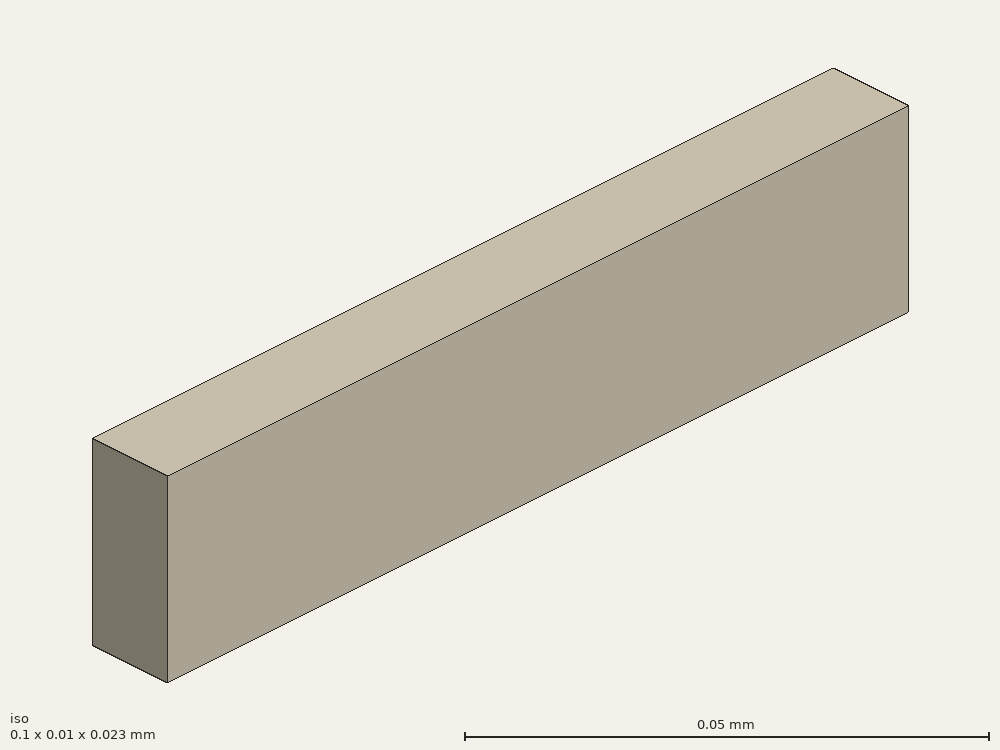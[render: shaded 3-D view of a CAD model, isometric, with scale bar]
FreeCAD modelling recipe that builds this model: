
FCSTD DOCUMENT  (FreeCAD 0.21R33694 (Git))
Label: straight-rotated
License: All rights reserved
LicenseURL: http://en.wikipedia.org/wiki/All_rights_reserved
objects: Part::Part2DObjectPython×5, App::FeaturePython×4, Part::Extrusion×1
note: 6 computed .brp shape members not serialized (recipe doc carries the construction recipe); baked Part::Feature solids carry a one-line shape summary decoded from their .brp

FEATURE [Part::Part2DObjectPython] Rectangle001  label="_Pport1"  # Draft 2D object (typed FeaturePython)
  Area = 0.000232258
  ChamferSize = 0
  Columns = 1
  FilletRadius = 0
  Height = 0.01016
  Length = 0.02286
  MakeFace = true
  Placement = pos=(-0.1,-0.00508,-0.01143) rot=(0,-1,0;1.5708rad)
  Rows = 1
FEATURE [Part::Part2DObjectPython] Line  label="_Pv1"  # Draft 2D object (typed FeaturePython)
  Area = 0
  ChamferSize = 0
  Closed = false
  End = (-0.1,0.00508,-1.8e-15)
  FilletRadius = 0
  Length = 0.01016
  MakeFace = true
  Placement = pos=(-0.1,-0.00508,0) rot=(0,-1,0;1.5708rad)
  Points = (2) [(0,0,0),(-1.77605e-15,0.01016,0)]
  Start = (-0.1,-0.00508,0)
  Subdivisions = 0
FEATURE [Part::Part2DObjectPython] Rectangle002  label="_Pport2"  # Draft 2D object (typed FeaturePython)
  Area = 0.000232258
  ChamferSize = 0
  Columns = 1
  FilletRadius = 0
  Height = 0.01016
  Length = 0.02286
  MakeFace = true
  Placement = pos=(0,-0.00508,-0.01143) rot=(0,-1,0;1.5708rad)
  Rows = 1
FEATURE [Part::Part2DObjectPython] Line001  label="_Pv2"  # Draft 2D object (typed FeaturePython)
  Area = 0
  ChamferSize = 0
  Closed = false
  End = (0,0.00508,0)
  FilletRadius = 0
  Length = 0.01016
  MakeFace = true
  Placement = pos=(0,-0.00508,0) rot=(0,-1,0;1.5708rad)
  Points = (2) [(0,0,0),(3.1106e-19,0.01016,0)]
  Start = (0,-0.00508,0)
  Subdivisions = 0
FEATURE [App::FeaturePython] Text  label="_S1(PV){port1}"  # WARN: FeaturePython — macro-defined, semantics opaque (R4)
  Placement = pos=(0.0413747,-0.017509,0) rot=(0,0,1;0rad)
  Text = .
FEATURE [App::FeaturePython] Text001  label="_S2(PV){port2}"  # WARN: FeaturePython — macro-defined, semantics opaque (R4)
  Placement = pos=(0.0413747,-0.017509,0) rot=(0,0,1;0rad)
  Text = .
FEATURE [App::FeaturePython] Text002  label="_L1(1,voltage){v1}"  # WARN: FeaturePython — macro-defined, semantics opaque (R4)
  Placement = pos=(0.0413747,-0.017509,0) rot=(0,0,1;0rad)
  Text = .
FEATURE [App::FeaturePython] Text003  label="_L2(2,voltage){v2}"  # WARN: FeaturePython — macro-defined, semantics opaque (R4)
  Placement = pos=(0.0413747,-0.017509,0) rot=(0,0,1;0rad)
  Text = .
FEATURE [Part::Part2DObjectPython] Rectangle003  # Draft 2D object (typed FeaturePython)
  Area = 0.000232258
  ChamferSize = 0
  Columns = 1
  FilletRadius = 0
  Height = 0.02286
  Length = 0.01016
  MakeFace = true
  Placement = pos=(0,-0.00508,-0.01143) rot=(0.57735,0.57735,0.57735;2.0944rad)
  Rows = 1
FEATURE [Part::Extrusion] Extrude001  label="Extrude002"
  Base = -> Rectangle003
  Dir = (1,0,0)
  DirMode = 2
  FaceMakerClass = Part::FaceMakerBullseye
  LengthFwd = -0.1
  LengthRev = 0
  Solid = false
  Symmetric = false
